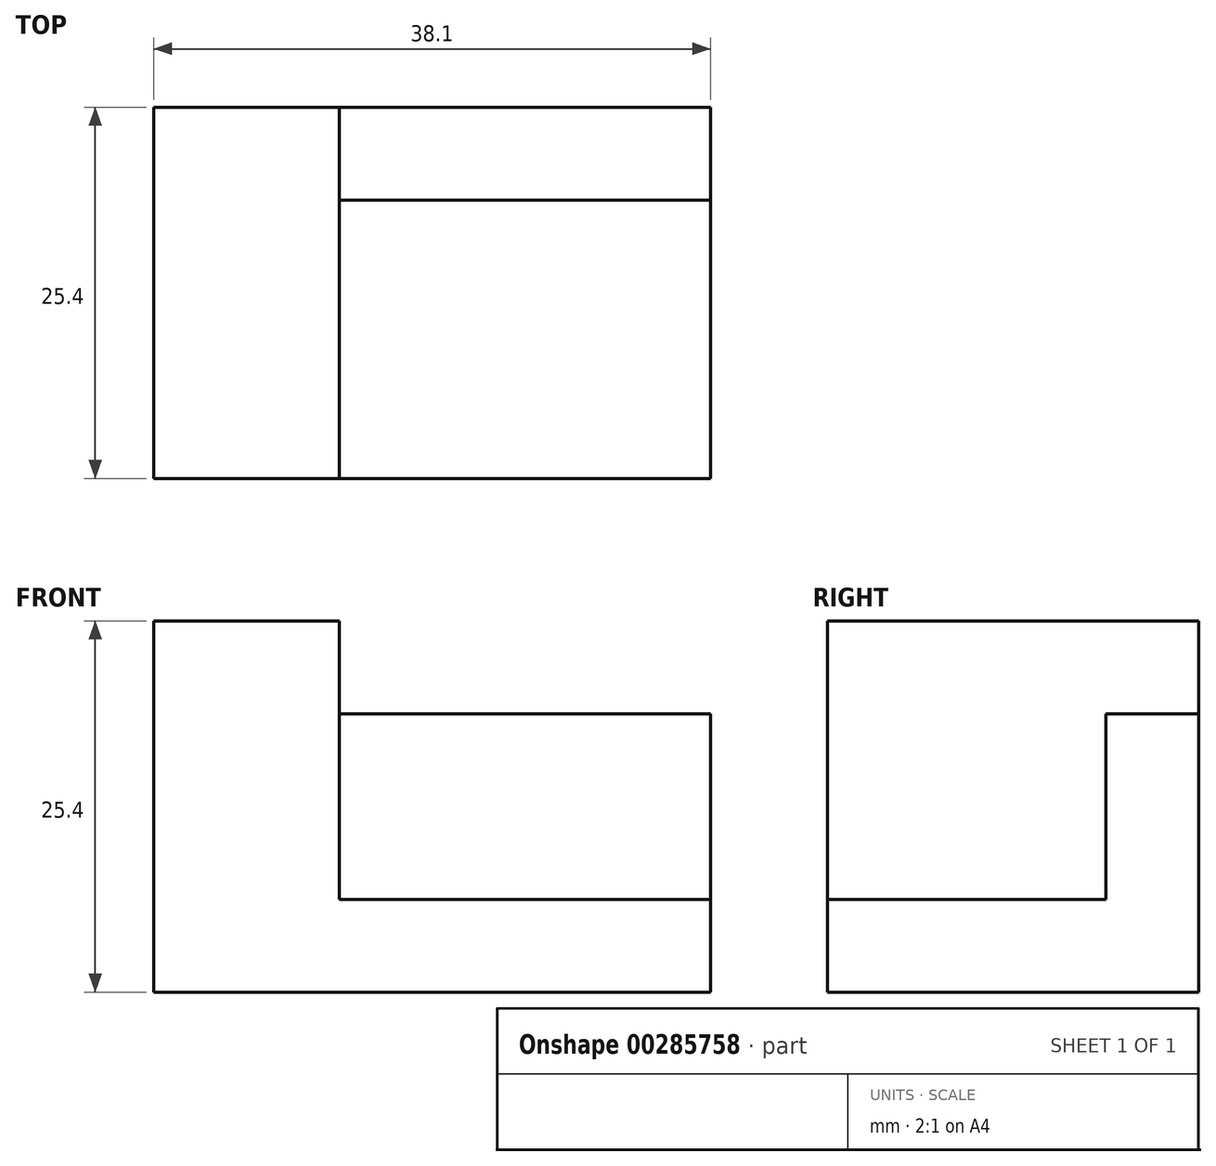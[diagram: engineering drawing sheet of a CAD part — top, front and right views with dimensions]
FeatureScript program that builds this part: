
annotation { "Feature Type Name" : "Feature", "Feature Type Description" : "" }
export const myFeature = defineFeature(function(context is Context, id is Id, definition is map)
    precondition{}
    {
        {
            var Q0;
            Q0=qCreatedBy(makeId("Right.planeOp"),FACE);
            var sketch = newSketch(context, id + "F0", { "sketchPlane" : qUnion([Q0])});
            skLineSegment(sketch, "E0", {"start": v(0, 0) * mm, "end": v(-19.05, 0) * mm});
            skLineSegment(sketch, "E1", {"start": v(-19.05, 0) * mm, "end": v(-19.05, -6.35) * mm});
            skLineSegment(sketch, "E2", {"start": v(-19.05, -6.35) * mm, "end": v(6.35, -6.35) * mm});
            skLineSegment(sketch, "E3", {"start": v(6.35, -6.35) * mm, "end": v(6.35, 12.7) * mm});
            skLineSegment(sketch, "E4", {"start": v(6.35, 12.7) * mm, "end": v(0, 12.7) * mm});
            skLineSegment(sketch, "E5", {"start": v(0, 12.7) * mm, "end": v(0, 0) * mm});
            skSolve(sketch);
        }
        {
            var Q0;
            Q0 = qSketchRegion(id + "F0", true);
            extrude(context, id + "F1", {"entities" : qUnion([Q0]), "depth" : 25.4 * mm});
        }
        {
            var Q0;
            Q0=makeQuery(id+"F1.opExtrude","CAP_FACE",FACE,{"disambiguationData":[OSD([sQuery(id+"F0.wireOp",EDGE,"E0"),sQuery(id+"F0.wireOp",EDGE,"E1"),sQuery(id+"F0.wireOp",EDGE,"E2"),sQuery(id+"F0.wireOp",EDGE,"E3"),sQuery(id+"F0.wireOp",EDGE,"E4"),sQuery(id+"F0.wireOp",EDGE,"E5")])],"isStart":true});
            var sketch = newSketch(context, id + "F2", { "sketchPlane" : qUnion([Q0])});
            skLineSegment(sketch, "E6.bottom", {"start": v(-6.35, -6.35) * mm, "end": v(19.05, -6.35) * mm});
            skLineSegment(sketch, "E6.top", {"start": v(-6.35, 19.05) * mm, "end": v(19.05, 19.05) * mm});
            skLineSegment(sketch, "E6.left", {"start": v(-6.35, -6.35) * mm, "end": v(-6.35, 19.05) * mm});
            skLineSegment(sketch, "E6.right", {"start": v(19.05, -6.35) * mm, "end": v(19.05, 19.05) * mm});
            skSolve(sketch);
        }
        {
            var Q0;
            Q0 = qSketchRegion(id + "F2", true);
            extrude(context, id + "F3", {"entities" : qUnion([Q0]), "operationType" : NewBodyOperationType.ADD, "depth" : 12.7 * mm});
        }
    });
